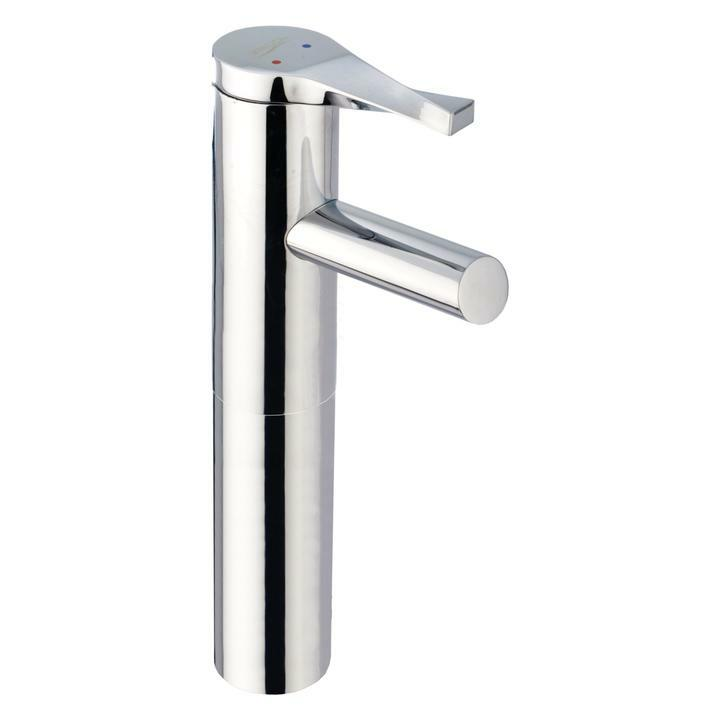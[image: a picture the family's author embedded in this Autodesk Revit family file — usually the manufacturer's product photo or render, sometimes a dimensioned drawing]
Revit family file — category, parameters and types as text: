
# Revit family: 01-2606-11-GRICOL MONOMANDO LAVAMANOS ALTO SION
name_source: partatom
category: Plumbing Fixtures
revit_build: Autodesk Revit 2018 (Build: 20170223_1515(x64)
units: mm (PartAtom-declared; Revit-internal decimal feet)

## family parameters
Cut with Voids When Loaded = No
Host = Face
OmniClass Number = 23.31.11.00
Part Type = Normal
Room Calculation Point = No
Round Connector Dimension = Use Diameter
Shared = No

## types (2) — shared parameters
Alto = 152 mm
Ancho = 50 mm  [stored 0.164042 ft]
CW Connection = Yes
Description = Griferia Monomando baño
Flow Rate = 2 GPM
HW Connection = Yes
Largo = 110 mm  [stored 0.360892 ft]
Link Ficha Tecnica = http://infotecnica.gricol.com
Manufacturer = Gricol
Metal Zamak Cromado = Metal Zamak Cromado
Model = 01-2606-11
Plastico ABS Cromado = Plastico ABS Cromado
Pressure = 60.00 psi
Product Name = MONOMANDO LAVAMANOS ALTO SION
Type Image = <None>
URL = https://www.gricol.com
Vent Connection = No
Waste Connection = No
zero-valued in all types: Default Elevation

## type names (no varying parameters)
- 01-2606-11
- 01-2603-11

note: [stored X ft] marks values corroborated as IEEE doubles in the binary element streams (Revit-internal decimal feet)

## geometry (parser evidence)
native form markers: Blend x2, Sweep x4
no freeform markers — native parametric forms only
